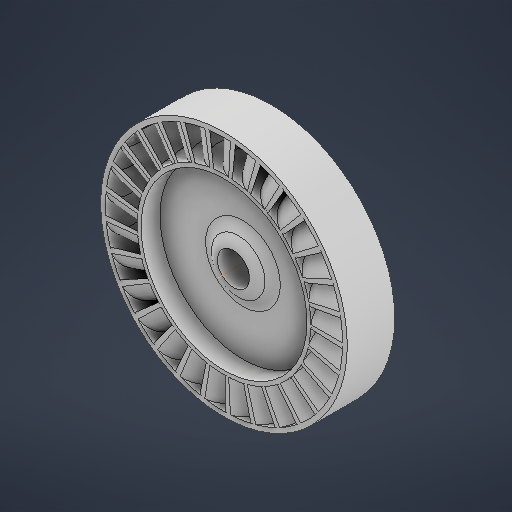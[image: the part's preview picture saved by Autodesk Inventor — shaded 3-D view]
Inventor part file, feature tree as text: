
AUTODESK INVENTOR PART (.ipt)
format: ipt  version: 2025.3 (Build 293356030, 356C)  size: 567,808 bytes
history: native  units: mm
features: sketch x5, extrude x5, sweep x1, pattern_circular x1, other x1, revolve x1
ambient origin geometry x8: Origin, YZ Plane, XZ Plane, XY Plane, X Axis, Y Axis, Z Axis, Center Point
bodies: Solid1 (feature_tree)
feature tree (14):
  sketch  "Sketch1"  dims[d0=36.6mm d1=50.0mm]
  extrude  "Extrusion1"  Depth=50.0mm
  extrude  "Extrusion2"  Depth=10.0mm TaperAngle=0.0deg
  sketch  "Sketch2"  dims[d2=2.0mm d3=0.0mm d4=10.0mm d5=0.0mm]
  sweep  "Sweep1"
  pattern_circular  "Circular Pattern1"  Count=29 Angle=360.0deg
  extrude  "Extrusion3"  Depth=10.0mm
  extrude  "Extrusion4"  Depth=10.0mm TaperAngle=0.0deg
  extrude  "Extrusion5"  Depth=10.0mm TaperAngle=0.0deg
  other  "Work Axis1"
  revolve  "Revolution1"  [1 undecoded]
  sketch  "Sketch7"  dims[d6=1.745329mm d7=0.0mm d8=0.0mm]
  sketch  "Sketch8"  dims[d10=1.0mm d11=290.0mm d12=360.0deg]
  sketch  "Sketch9"  dims[d14=35.0mm d15=52.0mm d16=10.0mm d17=0.0mm d18=10.0mm d19=0.0mm d20=6.8mm d21=0.0mm d22=0.0mm d23=90.0deg]
note: 1 required parameter value undecoded (feature->parameter linkage not recoverable at this tier; creation-order binding heuristic only, values carry confidence <= 0.55)
